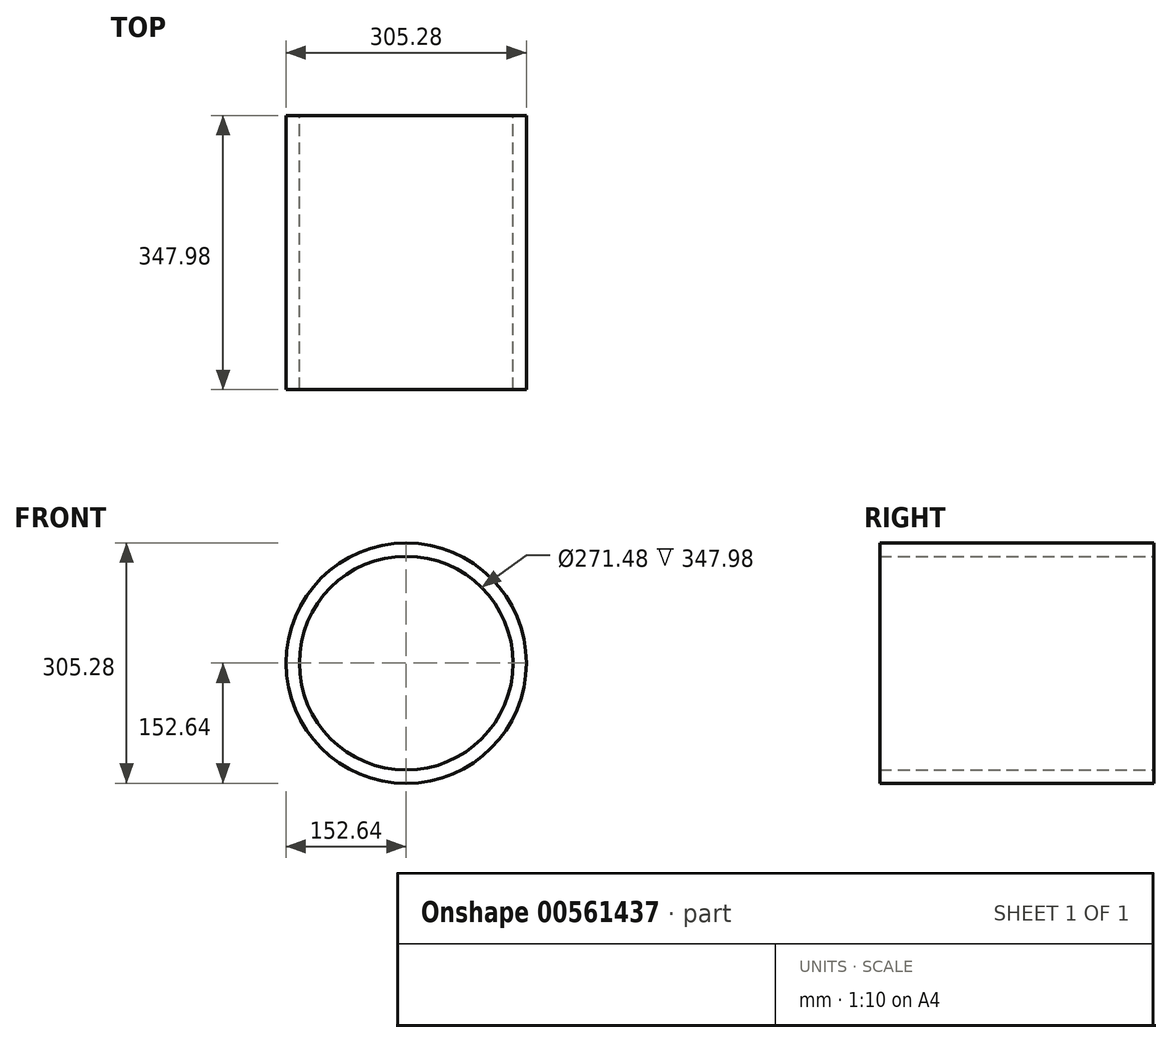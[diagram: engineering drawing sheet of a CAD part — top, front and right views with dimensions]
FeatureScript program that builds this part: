
annotation { "Feature Type Name" : "Feature", "Feature Type Description" : "" }
export const myFeature = defineFeature(function(context is Context, id is Id, definition is map)
    precondition{}
    {
        {
            var Q0;
            Q0=qCreatedBy(makeId("Front.planeOp"),FACE);
            var sketch = newSketch(context, id + "F0", { "sketchPlane" : qUnion([Q0])});
            skCircle(sketch, "E0", {"center": v(0, 0) * mm, "radius": 76.72 * mm});
            skCircle(sketch, "E1", {"center": v(0, 0) * mm, "radius": 67.73 * mm});
            skCircle(sketch, "E2", {"center": v(0, 0) * mm, "radius": 59.42 * mm});
            skCircle(sketch, "E3", {"center": v(0, 0) * mm, "radius": 52.43 * mm});
            skCircle(sketch, "E4", {"center": v(0, 0) * mm, "radius": 44.73 * mm});
            skCircle(sketch, "E5", {"center": v(0, 0) * mm, "radius": 36.43 * mm});
            skCircle(sketch, "E6", {"center": v(0, 0) * mm, "radius": 25.57 * mm});
            skCircle(sketch, "E7", {"center": v(0, 0) * mm, "radius": 14.06 * mm});
            skCircle(sketch, "E8", {"center": v(0, 0) * mm, "radius": 6.4 * mm});
            skCircle(sketch, "E9", {"center": v(0, 0) * mm, "radius": 88.2 * mm});
            skCircle(sketch, "E10", {"center": v(0, 0) * mm, "radius": 102.53 * mm});
            skCircle(sketch, "E11", {"center": v(0, 0) * mm, "radius": 118.59 * mm});
            skCircle(sketch, "E12", {"center": v(0, 0) * mm, "radius": 135.74 * mm});
            skCircle(sketch, "E13", {"center": v(0, 0) * mm, "radius": 152.64 * mm});
            skSolve(sketch);
        }
        {
            var Q0;
            Q0 = qSketchRegion(id + "F0", true);
            extrude(context, id + "F1", {"entities" : qUnion([Q0]), "depth" : 347.98 * mm, "offsetDistance" : 25.4 * mm});
        }
    });
